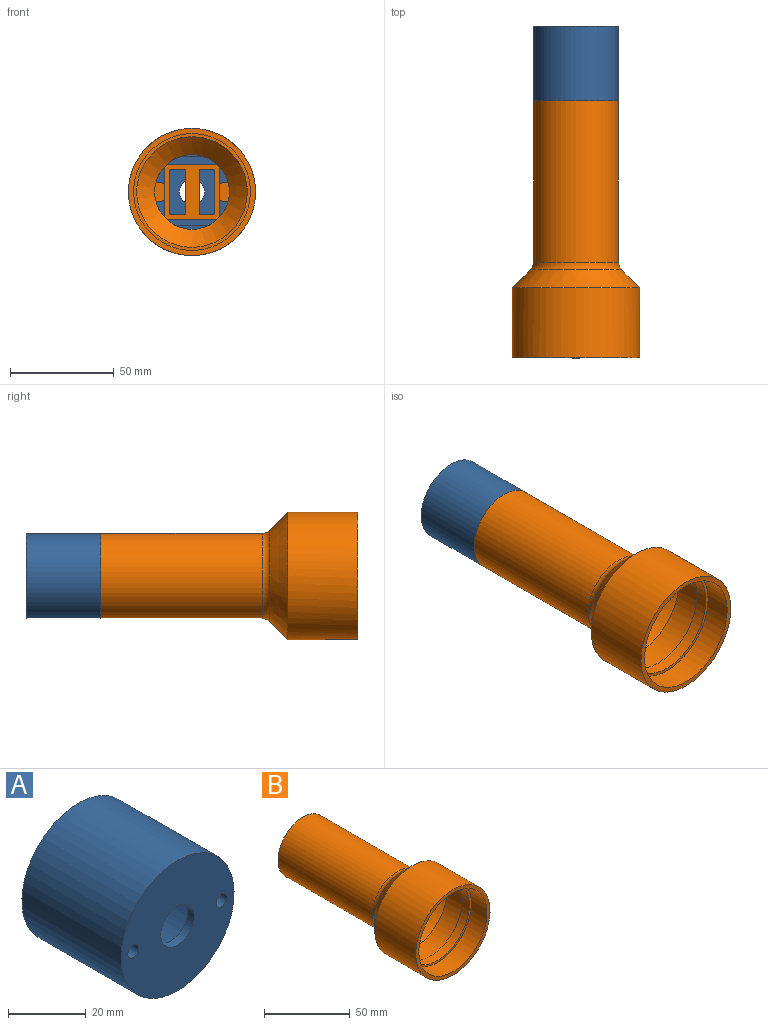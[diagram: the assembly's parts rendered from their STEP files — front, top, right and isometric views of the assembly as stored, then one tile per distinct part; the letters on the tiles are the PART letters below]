
ASSEMBLY  parts=2 mates=1
PART A: 19 faces, bbox 41x37.5x41 mm
  f0: plane 41x41mm, normal (0,1,0), area 372.3mm2, adj f1,f2,f4,f6,f7,f8,f9,f11
  f1: cylinder r=2mm len=36mm, axis (0,1,0), area 452.4mm2, adj f0,f5
  f2: cylinder r=2mm len=36mm, axis (0,1,0), area 452.4mm2, adj f0,f5
  f3: cylinder r=6.1mm len=12.2mm, axis (0,1,0), area 95.8mm2, adj f5,f10
  f4: cylinder r=20.5mm len=41mm, axis (0,1,0), area 4637mm2, adj f0,f5
  f5: plane 41x41mm, normal (0,-1,0), area 1178.2mm2, adj f1,f2,f3,f4
  f6: cylinder r=18mm len=34.98mm, axis (0,1,0), area 1545.8mm2, adj f0,f7,f8,f10,f12,f18
  f7: cylinder r=4.5mm len=33.5mm, axis (0,1,0), area 571.2mm2, adj f0,f6,f9,f10
  f8: cylinder r=4.5mm len=33.5mm, axis (0,1,0), area 574mm2, adj f0,f6,f9,f10
  f9: cylinder r=18mm len=34.98mm, axis (0,1,0), area 1571.2mm2, adj f0,f7,f8,f10,f15,f17
  f10: plane 36x34.98mm, normal (0,1,0), area 805.9mm2, adj f3,f6,f7,f8,f9
  f11: cylinder r=18mm len=15.85mm, axis (0,-1,0), area 24.6mm2, adj f0,f12,f13
  f12: plane 15.85x2.9mm, normal (0,0,-1), area 46mm2, adj f6,f11,f13,f18
  f13: plane 15.85x1.84mm, normal (0,1,0), area 19.6mm2, adj f11,f12
  f14: cylinder r=18mm len=11.12mm, axis (0,-1,0), area 17mm2, adj f0,f15,f16
  f15: plane 11.12x2.9mm, normal (0,0,1), area 32.2mm2, adj f9,f14,f16,f17
  f16: plane 11.12x0.88mm, normal (0,1,0), area 6.6mm2, adj f14,f15
  f17: cylinder r=3mm len=11.12mm, axis (1,0,0), area 20.5mm2, adj f9,f15
  f18: cylinder r=3mm len=15.85mm, axis (-1,0,0), area 43.5mm2, adj f6,f12
PART B: 68 faces, bbox 61.3x124x61.3 mm
  f0: plane 81x23.81mm, normal (0,0,1), area 508.8mm2, adj f2,f14,f19,f41,f43,f46,f65
  f1: cylinder r=18mm len=81mm, axis (0,1,0), area 1198.9mm2, adj f13,f37,f39,f46
  f2: cylinder r=18mm len=81mm, axis (0,1,0), area 188.8mm2, adj f0,f13,f40,f46,f66
  f3: plane 81x23.81mm, normal (1,0,0), area 1831.5mm2, adj f6,f19,f29,f30,f31,f46
  f4: plane 81x22mm, normal (0,0,1), area 1769.4mm2, adj f19,f20,f24,f26,f27,f28,f46
  f5: cylinder r=18mm len=81mm, axis (0,1,0), area 2107.5mm2, adj f13,f23,f46
  f6: cylinder r=18mm len=81mm, axis (0,1,0), area 1996.1mm2, adj f3,f13,f29,f30,f31,f46
  f7: cylinder r=18mm len=81mm, axis (0,1,0), area 1996.1mm2, adj f13,f22,f32,f33,f34,f46
  f8: cylinder r=28.15mm len=56.3mm, axis (0,1,0), area 2299.3mm2, adj f9,f18
  f9: plane 56.3x56.3mm, normal (0,-1,0), area 258.2mm2, adj f8,f10
  f10: cylinder r=26.65mm len=53.3mm, axis (0,1,0), area 1004.7mm2, adj f9,f11
  f11: plane 56.3x56.3mm, normal (0,1,0), area 258.2mm2, adj f10,f12
  f12: cylinder r=28.15mm len=56.3mm, axis (0,1,0), area 2449.7mm2, adj f11,f13
  f13: cone r=18mm half-angle=45deg, axis (0,-1,0), area 2081.1mm2, adj f1,f2,f5,f6,f7,f12,f14,f19
  f14: cylinder r=18mm len=81mm, axis (0,1,0), area 201.6mm2, adj f0,f13,f36,f46,f67
  f15: cylinder r=20.5mm len=77.89mm, axis (0,1,0), area 10033.1mm2, adj f25,f46
  f16: cone r=20.5mm half-angle=45deg, axis (0,-1,0), area 2030.3mm2, adj f17,f25
  f17: cylinder r=30.65mm len=61.3mm, axis (0,1,0), area 6525.7mm2, adj f16,f18
  f18: plane 61.3x61.3mm, normal (0,-1,0), area 461.8mm2, adj f8,f17
  f19: plane 27x27mm, normal (0,-1,0), area 394.6mm2, adj f0,f3,f4,f13,f20,f21,f22,f23
  f20: plane 81x21mm, normal (1,0,0), area 1701mm2, adj f4,f19,f44,f46
  f21: plane 81x20mm, normal (0,0,-1), area 1607.4mm2, adj f19,f26,f27,f28,f44,f45,f46
  f22: plane 81x23.81mm, normal (-1,0,0), area 1831.5mm2, adj f7,f19,f32,f33,f34,f46
  f23: plane 81x23.81mm, normal (0,0,-1), area 1928.8mm2, adj f5,f19,f46
  f24: plane 81x21mm, normal (-1,0,0), area 1701mm2, adj f4,f19,f45,f46
  f25: torus R=25.5mm, axis (0,1,0), area 518.1mm2, adj f15,f16
  f26: plane 22x1.8mm, normal (-1,0,0), area 39.6mm2, adj f4,f19,f21,f28
  f27: plane 22x1.8mm, normal (1,0,0), area 39.6mm2, adj f4,f19,f21,f28
  f28: plane 22x7mm, normal (0,1,0), area 154mm2, adj f4,f21,f26,f27
  f29: cylinder r=4.5mm len=13mm, axis (0,1,0), area 54.2mm2, adj f3,f6,f31,f46
  f30: cylinder r=4.5mm len=13mm, axis (0,1,0), area 54.2mm2, adj f3,f6,f31,f46
  f31: plane 9x4.5mm, normal (0,-1,0), area 37.3mm2, adj f3,f6,f29,f30
  f32: cylinder r=4.5mm len=13mm, axis (0,1,0), area 54.2mm2, adj f7,f22,f34,f46
  f33: cylinder r=4.5mm len=13mm, axis (0,1,0), area 54.2mm2, adj f7,f22,f34,f46
  f34: plane 9x4.5mm, normal (0,-1,0), area 37.3mm2, adj f7,f22,f32,f33
  f35: plane 1.74x0.87mm, normal (0,1,0), area 0.7mm2, adj f13,f37,f67
  f36: plane 80x1.49mm, normal (1,0,0), area 119.2mm2, adj f14,f37,f46,f67
  f37: plane 81x2.74mm, normal (0,0,-1), area 221.8mm2, adj f1,f35,f36,f46,f67
  f38: plane 1.87x0.95mm, normal (0,1,0), area 0.8mm2, adj f13,f39,f66
  f39: plane 81x2.87mm, normal (0,0,-1), area 232.4mm2, adj f1,f38,f40,f46,f66
  f40: plane 80x1.58mm, normal (-1,0,0), area 126.2mm2, adj f2,f39,f46,f66
  f41: plane 71x1.4mm, normal (-1,0,0), area 97.9mm2, adj f0,f42,f46,f65
  f42: plane 67.53x20mm, normal (0,0,1), area 1350.6mm2, adj f41,f43,f46,f65
  f43: plane 71x1.4mm, normal (1,0,0), area 97.9mm2, adj f0,f42,f46,f65
  f44: cylinder r=1mm len=81mm, axis (0,-1,0), area 127.2mm2, adj f19,f20,f21,f46
  f45: cylinder r=1mm len=81mm, axis (0,1,0), area 127.2mm2, adj f19,f21,f24,f46
  f46: plane 41x41mm, normal (0,1,0), area 566.4mm2, adj f0,f1,f2,f3,f4,f5,f6,f7
  f47: plane 5.6x4.85mm, normal (0,-1,0), area 10.7mm2, adj f48,f50,f51,f52,f53,f54,f55
  f48: cylinder r=1.75mm len=3.5mm, axis (0,1,0), area 11mm2, adj f46,f47
  f49: plane 5.6x4.85mm, normal (0,1,0), area 20.4mm2, adj f50,f51,f52,f53,f54,f55
  f50: plane 6.4x2.8mm, normal (0,0,1), area 17.9mm2, adj f47,f49,f51,f55
  f51: plane 6.4x2.43mm, normal (-0.87,0,0.5), area 17.9mm2, adj f47,f49,f50,f52
  f52: plane 6.4x2.43mm, normal (-0.87,0,-0.5), area 17.9mm2, adj f47,f49,f51,f53
  f53: plane 6.4x2.8mm, normal (0,0,-1), area 17.9mm2, adj f47,f49,f52,f54
  f54: plane 6.4x2.43mm, normal (0.87,0,-0.5), area 17.9mm2, adj f47,f49,f53,f55
  f55: plane 6.4x2.43mm, normal (0.87,0,0.5), area 17.9mm2, adj f47,f49,f50,f54
  f56: plane 5.6x4.85mm, normal (0,-1,0), area 10.7mm2, adj f57,f59,f60,f61,f62,f63,f64
  f57: cylinder r=1.75mm len=3.5mm, axis (0,1,0), area 11mm2, adj f46,f56
  f58: plane 5.6x4.85mm, normal (0,1,0), area 20.4mm2, adj f59,f60,f61,f62,f63,f64
  f59: plane 6.4x2.8mm, normal (0,0,1), area 17.9mm2, adj f56,f58,f60,f64
  f60: plane 6.4x2.43mm, normal (-0.87,0,0.5), area 17.9mm2, adj f56,f58,f59,f61
  f61: plane 6.4x2.43mm, normal (-0.87,0,-0.5), area 17.9mm2, adj f56,f58,f60,f62
  f62: plane 6.4x2.8mm, normal (0,0,-1), area 17.9mm2, adj f56,f58,f61,f63
  f63: plane 6.4x2.43mm, normal (0.87,0,-0.5), area 17.9mm2, adj f56,f58,f62,f64
  f64: plane 6.4x2.43mm, normal (0.87,0,0.5), area 17.9mm2, adj f56,f58,f59,f63
  f65: cylinder r=5mm len=20mm, axis (1,0,0), area 76.7mm2, adj f0,f41,f42,f43
  f66: cylinder r=1mm len=1.58mm, axis (0,0,-1), area 2.1mm2, adj f2,f38,f39,f40
  f67: cylinder r=1mm len=1.49mm, axis (0,0,1), area 2mm2, adj f14,f35,f36,f37
PLACE A rot(axis=(1,0,0),180deg) t=(0,-46,0)mm
PLACE B at identity fixed
MATE fastened B.f1 <-> A.f4  axis (0,1,0) through (0,-46,0)mm
